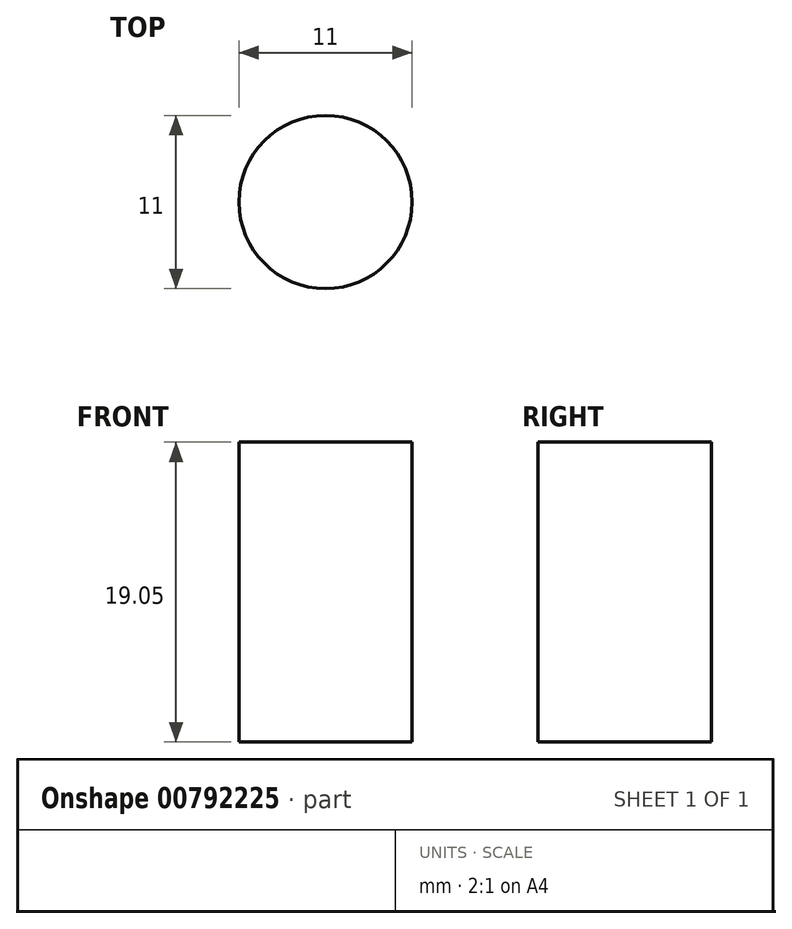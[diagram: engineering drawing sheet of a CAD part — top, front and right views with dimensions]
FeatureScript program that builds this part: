
annotation { "Feature Type Name" : "Feature", "Feature Type Description" : "" }
export const myFeature = defineFeature(function(context is Context, id is Id, definition is map)
    precondition{}
    {
        {
            var Q0;
            Q0=qCreatedBy(makeId("Top.planeOp"),FACE);
            var sketch = newSketch(context, id + "F0", { "sketchPlane" : qUnion([Q0])});
            skCircle(sketch, "E0", {"center": v(0, 0) * mm, "radius": 5.5 * mm});
            skSolve(sketch);
        }
        {
            var Q0;
            Q0=makeQuery(id+"F0.imprint","IMPRINT",FACE,{"disambiguationData":[TD([[makeQuery(id+"F0.imprint","IMPRINT",EDGE,{"derivedFrom":sQuery(id+"F0.wireOp",EDGE,"E0")}),1.0]])]});
            var Q1;
            Q1=sQuery(id+"F0.wireOp",EDGE,"E0");
            extrude(context, id + "F1", {"entities" : qUnion([Q0]), "surfaceEntities" : qUnion([Q1]), "depth" : 19.05 * mm, "offsetDistance" : 25.4 * mm});
        }
    });
